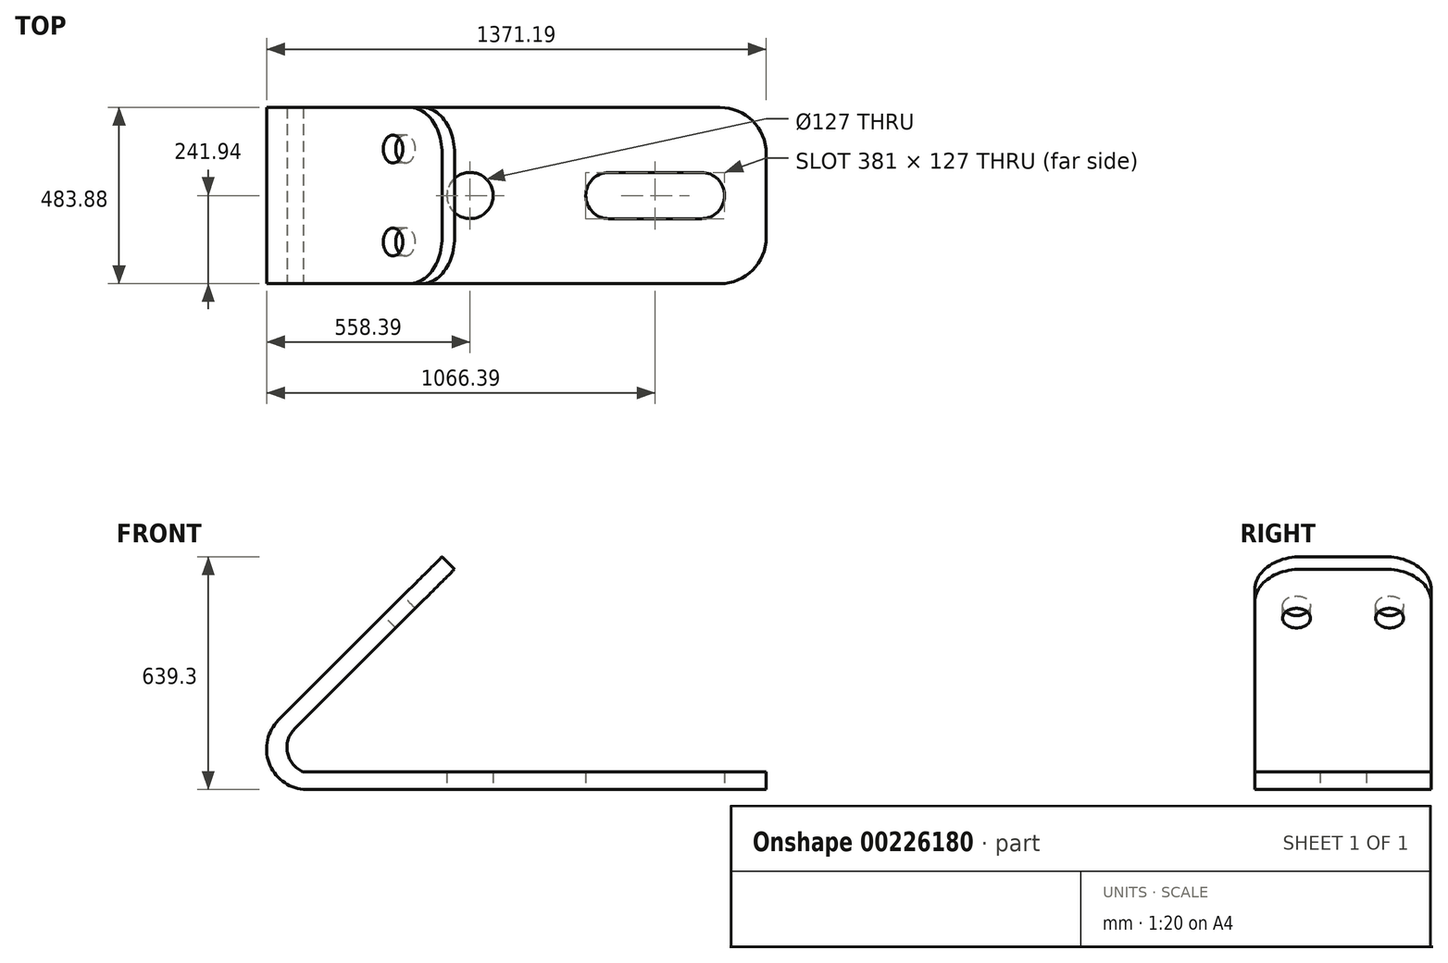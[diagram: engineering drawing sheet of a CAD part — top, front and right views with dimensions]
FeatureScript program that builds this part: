
annotation { "Feature Type Name" : "Feature", "Feature Type Description" : "" }
export const myFeature = defineFeature(function(context is Context, id is Id, definition is map)
    precondition{}
    {
        {
            var Q0;
            Q0=qCreatedBy(makeId("Top.planeOp"),FACE);
            var sketch = newSketch(context, id + "F0", { "sketchPlane" : qUnion([Q0])});
            skLineSegment(sketch, "E0.left", {"start": v(635, -114.94) * mm, "end": v(635, 114.94) * mm});
            skPoint(sketch, "E0.middle", {"position": v(0, 0) * mm});
            skArc(sketch, "E1", {"start": v(635, 114.94) * mm, "mid": v(597.8, 204.74) * mm, "end": v(508, 241.94) * mm});
            skArc(sketch, "E2", {"start": v(508, -241.94) * mm, "mid": v(597.8, -204.74) * mm, "end": v(635, -114.94) * mm});
            skLineSegment(sketch, "E3", {"start": v(508, 241.94) * mm, "end": v(-635, 241.93) * mm});
            skLineSegment(sketch, "E4", {"start": v(-635, 241.93) * mm, "end": v(-635, -241.94) * mm});
            skLineSegment(sketch, "E5", {"start": v(-635, -241.94) * mm, "end": v(508, -241.94) * mm});
            skLineSegment(sketch, "E6", {"start": v(508, 241.94) * mm, "end": v(508, -241.94) * mm, "construction": true});
            skCircle(sketch, "E7", {"center": v(-177.8, 0) * mm, "radius": 63.5 * mm});
            skCircle(sketch, "E8", {"center": v(457.2, 0) * mm, "radius": 63.5 * mm});
            skCircle(sketch, "E9", {"center": v(203.2, 0) * mm, "radius": 63.5 * mm});
            skLineSegment(sketch, "E10", {"start": v(203.2, 63.5) * mm, "end": v(457.2, 63.5) * mm});
            skLineSegment(sketch, "E11", {"start": v(457.2, -63.5) * mm, "end": v(203.2, -63.5) * mm});
            skSolve(sketch);
        }
        {
            var Q0;
            Q0=makeQuery(id+"F0.imprint","IMPRINT",FACE,{"disambiguationData":[TD([[makeQuery(id+"F0.imprint","IMPRINT",EDGE,{"derivedFrom":sQuery(id+"F0.wireOp",EDGE,"E0.left")}),1.0]])]});
            extrude(context, id + "F1", {"entities" : qUnion([Q0]), "depth" : 48.26 * mm});
        }
        {
            var Q0;
            Q0=qCreatedBy(makeId("Front.planeOp"),FACE);
            var sketch = newSketch(context, id + "F2", { "sketchPlane" : qUnion([Q0])});
            skPoint(sketch, "E12.0", {"position": v(-635, 48.26) * mm});
            skPoint(sketch, "E13.0", {"position": v(-635, 0) * mm});
            skLineSegment(sketch, "E14.0", {"start": v(-635, 48.26) * mm, "end": v(-635, 0) * mm});
            skLineSegment(sketch, "E15", {"start": v(-703.46, 190.29) * mm, "end": v(-254.44, 639.3) * mm});
            skLineSegment(sketch, "E16", {"start": v(-254.44, 639.3) * mm, "end": v(-220.32, 605.17) * mm});
            skLineSegment(sketch, "E17", {"start": v(-220.32, 605.17) * mm, "end": v(-659.06, 166.44) * mm});
            skLineSegment(sketch, "E18", {"start": v(-659.06, 166.44) * mm, "end": v(-703.46, 190.29) * mm});
            skArc(sketch, "E19", {"start": v(-659.06, 166.44) * mm, "mid": v(-678.78, 100.88) * mm, "end": v(-635, 48.26) * mm});
            skArc(sketch, "E20", {"start": v(-703.46, 190.29) * mm, "mid": v(-729.6, 73.43) * mm, "end": v(-635, 0) * mm});
            skSolve(sketch);
        }
        {
            var Q0;
            Q0 = qSketchRegion(id + "F2", true);
            extrude(context, id + "F3", {"entities" : qUnion([Q0]), "operationType" : NewBodyOperationType.ADD, "endBound" : BoundingType.SYMMETRIC, "oppositeDirection" : true, "depth" : 483.87 * mm});
        }
        {
            var Q0;
            Q0=makeQuery(id+"F3.opExtrude","CAP_EDGE",EDGE,{"disambiguationData":[OSD([sQuery(id+"F2.wireOp",EDGE,"E16")])],"isStart":true});
            var Q1;
            Q1=makeQuery(id+"F3.opExtrude","CAP_EDGE",EDGE,{"disambiguationData":[OSD([sQuery(id+"F2.wireOp",EDGE,"E16")])],"isStart":false});
            fillet(context, id + "F4", {"entities" : qUnion([Q0, Q1]), "radius" : 127 * mm, "tangentPropagation" : true, "allowEdgeOverflow" : false});
        }
        {
            var Q0;
            Q0=makeQuery(id+"F3.opExtrude","SWEPT_FACE",FACE,{"disambiguationData":[OSD([sQuery(id+"F2.wireOp",EDGE,"E15")])]});
            var sketch = newSketch(context, id + "F5", { "sketchPlane" : qUnion([Q0])});
            skCircle(sketch, "E21", {"center": v(-127.64, 81.63) * mm, "radius": 38.1 * mm});
            skCircle(sketch, "E22", {"center": v(127.64, 81.63) * mm, "radius": 38.1 * mm});
            skLineSegment(sketch, "E23", {"start": v(-127.64, 81.63) * mm, "end": v(127.64, 81.63) * mm});
            skSolve(sketch);
        }
        {
            var Q0;
            Q0=makeQuery(id+"F5.imprint","IMPRINT",FACE,{"disambiguationData":[TD([[makeQuery(id+"F5.imprint","IMPRINT",EDGE,{"derivedFrom":sQuery(id+"F5.wireOp",EDGE,"E22")}),1.0]])]});
            var Q1;
            Q1=makeQuery(id+"F5.imprint","IMPRINT",FACE,{"disambiguationData":[TD([[makeQuery(id+"F5.imprint","IMPRINT",EDGE,{"derivedFrom":sQuery(id+"F5.wireOp",EDGE,"E21")}),1.0]])]});
            extrude(context, id + "F6", {"entities" : qUnion([Q0, Q1]), "operationType" : NewBodyOperationType.REMOVE, "oppositeDirection" : true, "depth" : 48.26 * mm});
        }
    });
